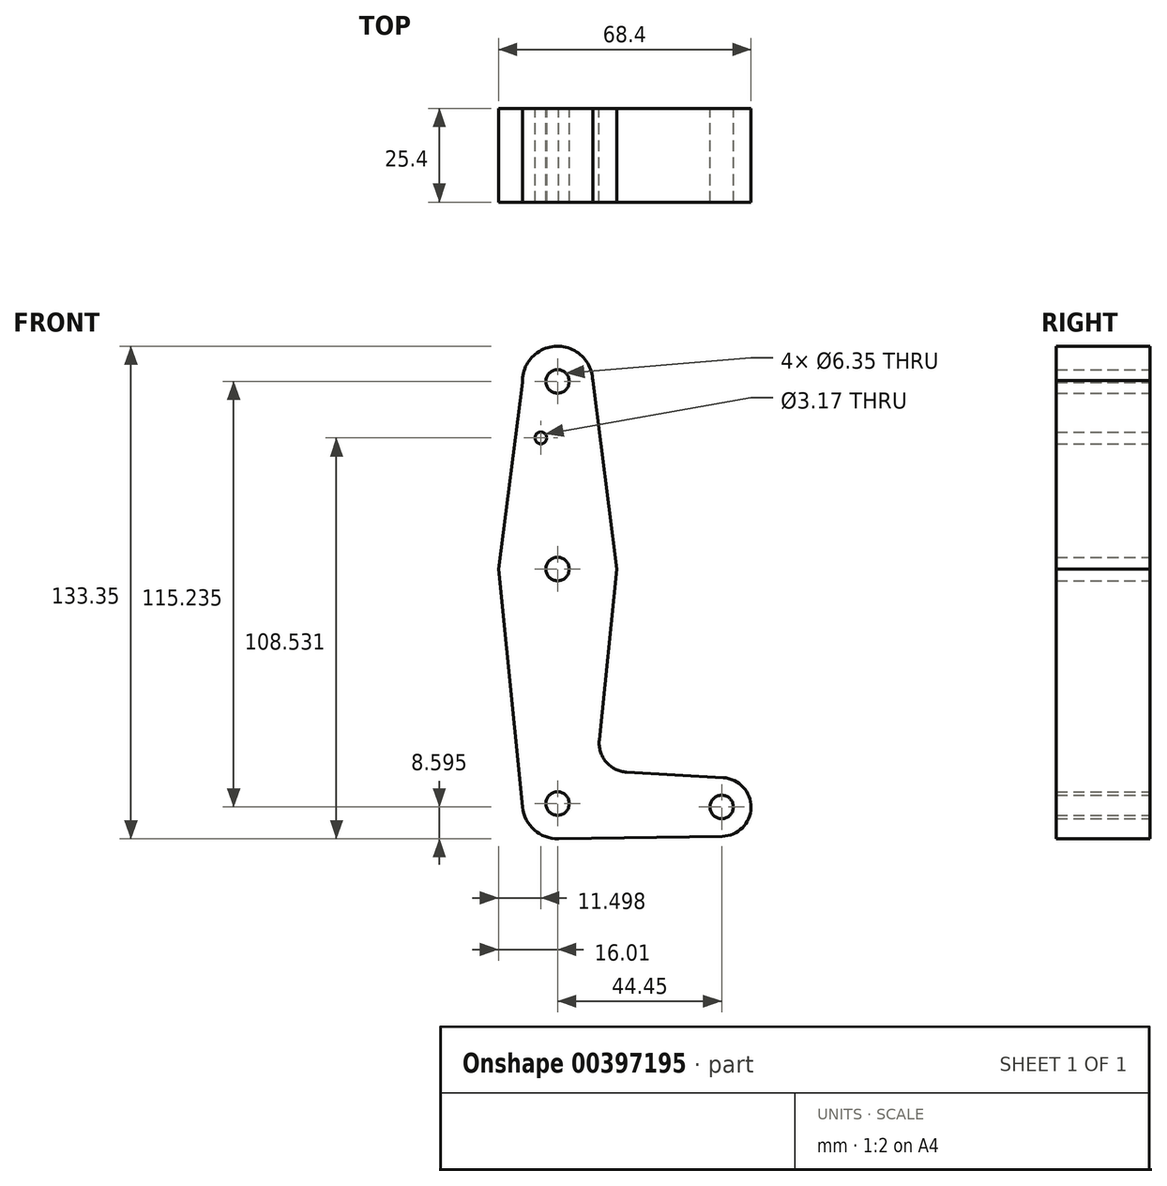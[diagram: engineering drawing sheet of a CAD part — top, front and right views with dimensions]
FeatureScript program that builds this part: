
annotation { "Feature Type Name" : "Feature", "Feature Type Description" : "" }
export const myFeature = defineFeature(function(context is Context, id is Id, definition is map)
    precondition{}
    {
        {
            var Q0;
            Q0=qCreatedBy(makeId("Front.planeOp"),FACE);
            var sketch = newSketch(context, id + "F0", { "sketchPlane" : qUnion([Q0])});
            skCircle(sketch, "E0", {"center": v(0, 50.8) * mm, "radius": 9.53 * mm});
            skCircle(sketch, "E1", {"center": v(0, 0) * mm, "radius": 15.88 * mm});
            skCircle(sketch, "E2", {"center": v(0, -63.5) * mm, "radius": 9.53 * mm});
            skCircle(sketch, "E3", {"center": v(44.45, -64.43) * mm, "radius": 7.94 * mm});
            skLineSegment(sketch, "E4", {"start": v(0, 50.8) * mm, "end": v(0, -63.5) * mm, "construction": true});
            skLineSegment(sketch, "E5", {"start": v(0, 0) * mm, "end": v(0, -63.5) * mm, "construction": true});
            skLineSegment(sketch, "E6", {"start": v(44.45, -64.43) * mm, "end": v(0, -63.5) * mm, "construction": true});
            skLineSegment(sketch, "E7", {"start": v(-9.52, 50.53) * mm, "end": v(-16, 0) * mm});
            skLineSegment(sketch, "E8", {"start": v(-16, 0) * mm, "end": v(-9.48, -64.46) * mm});
            skLineSegment(sketch, "E9", {"start": v(0, -73.03) * mm, "end": v(44.57, -72.37) * mm});
            skLineSegment(sketch, "E10", {"start": v(9.52, 50.98) * mm, "end": v(16, 0) * mm});
            skLineSegment(sketch, "E11", {"start": v(16, 0) * mm, "end": v(11.32, -46.3) * mm});
            skLineSegment(sketch, "E12", {"start": v(18.78, -55.04) * mm, "end": v(44.9, -56.51) * mm});
            skCircle(sketch, "E13", {"center": v(0, 50.8) * mm, "radius": 3.18 * mm});
            skCircle(sketch, "E14", {"center": v(0, 0) * mm, "radius": 3.18 * mm});
            skCircle(sketch, "E15", {"center": v(0, -63.5) * mm, "radius": 3.18 * mm});
            skCircle(sketch, "E16", {"center": v(44.45, -64.43) * mm, "radius": 3.18 * mm});
            skCircle(sketch, "E17", {"center": v(-4.51, 35.5) * mm, "radius": 1.59 * mm});
            skPoint(sketch, "E18.newPointB", {"position": v(0, -53.98) * mm});
            skArc(sketch, "E18.filletArc", {"start": v(11.32, -46.3) * mm, "mid": v(13.18, -52.26) * mm, "end": v(18.78, -55.04) * mm});
            skSolve(sketch);
        }
        {
            var Q0;
            Q0 = qSketchRegion(id + "F0", true);
            extrude(context, id + "F1", {"entities" : qUnion([Q0]), "depth" : 25.4 * mm});
        }
    });
